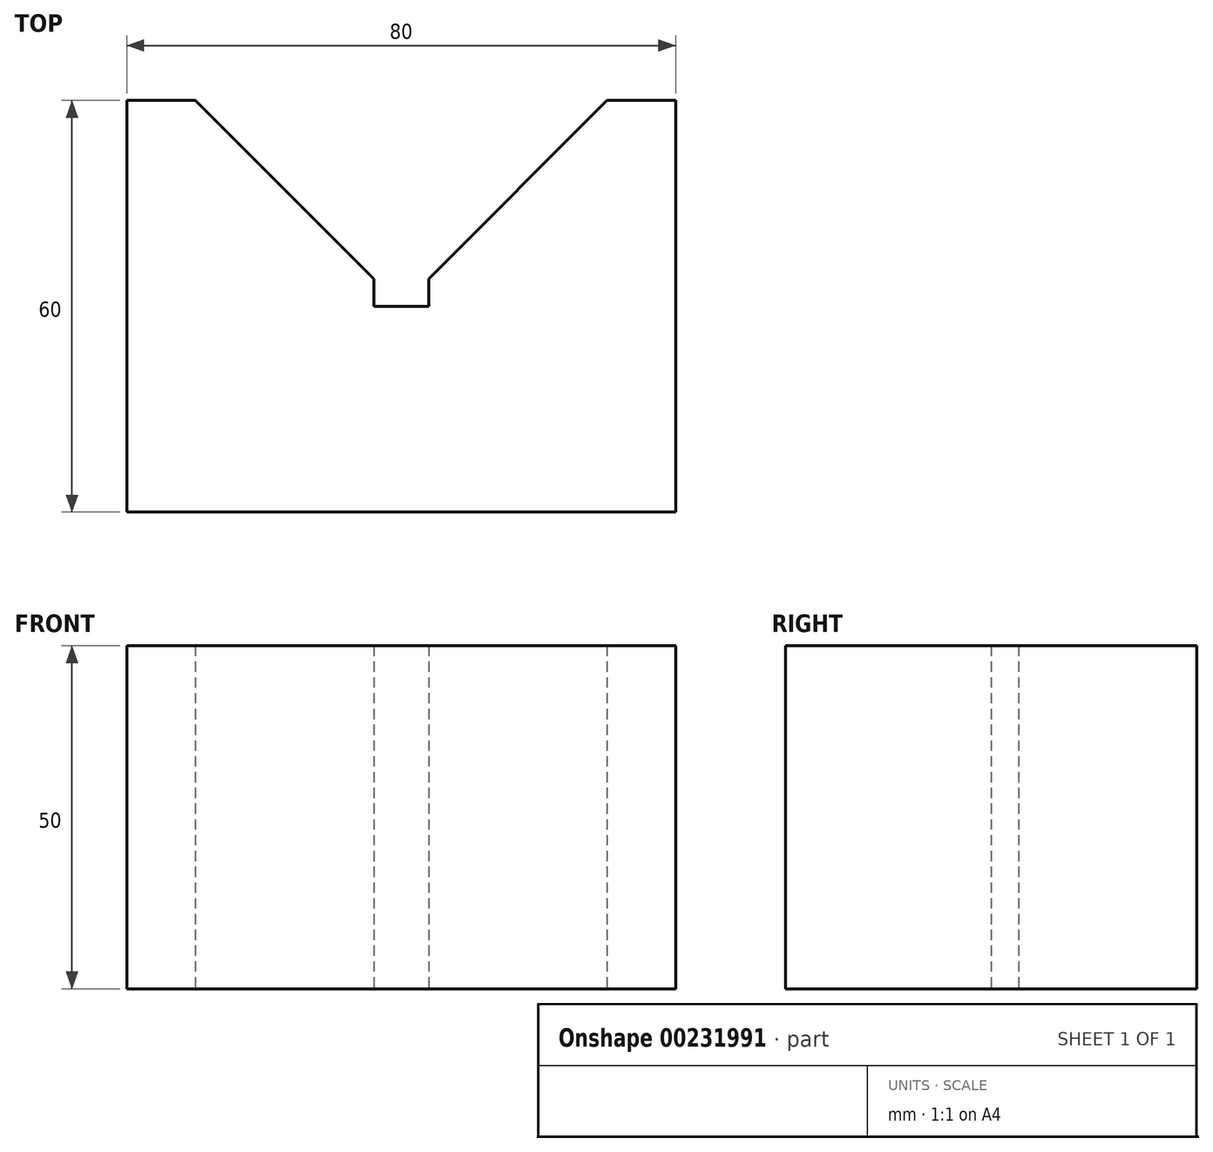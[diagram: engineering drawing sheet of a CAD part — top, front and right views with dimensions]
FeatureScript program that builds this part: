
annotation { "Feature Type Name" : "Feature", "Feature Type Description" : "" }
export const myFeature = defineFeature(function(context is Context, id is Id, definition is map)
    precondition{}
    {
        {
            var Q0;
            Q0=qCreatedBy(makeId("Top.planeOp"),FACE);
            var sketch = newSketch(context, id + "F0", { "sketchPlane" : qUnion([Q0])});
            skLineSegment(sketch, "E0", {"start": v(0, 0) * mm, "end": v(-40, 0) * mm});
            skLineSegment(sketch, "E1", {"start": v(-40, 0) * mm, "end": v(-40, 60) * mm});
            skLineSegment(sketch, "E2", {"start": v(-40, 60) * mm, "end": v(-30, 60) * mm});
            skLineSegment(sketch, "E3", {"start": v(-30, 60) * mm, "end": v(-4, 34) * mm});
            skLineSegment(sketch, "E4", {"start": v(-4, 34) * mm, "end": v(-4, 30) * mm});
            skLineSegment(sketch, "E5", {"start": v(-4, 30) * mm, "end": v(0, 30) * mm});
            skLineSegment(sketch, "E6.MirrorCS", {"start": v(4, 34) * mm, "end": v(4, 30) * mm});
            skLineSegment(sketch, "E7.MirrorCS", {"start": v(4, 30) * mm, "end": v(0, 30) * mm});
            skLineSegment(sketch, "E8.MirrorCS", {"start": v(0, 0) * mm, "end": v(40, 0) * mm});
            skLineSegment(sketch, "E9.MirrorCS", {"start": v(40, 60) * mm, "end": v(30, 60) * mm});
            skLineSegment(sketch, "E10.MirrorCS", {"start": v(40, 0) * mm, "end": v(40, 60) * mm});
            skLineSegment(sketch, "E11.MirrorCS", {"start": v(30, 60) * mm, "end": v(4, 34) * mm});
            skSolve(sketch);
        }
        {
            var Q0;
            Q0=makeQuery(id+"F0.imprint","IMPRINT",FACE,{"disambiguationData":[TD([[makeQuery(id+"F0.imprint","IMPRINT",EDGE,{"derivedFrom":sQuery(id+"F0.wireOp",EDGE,"E0")}),-1.0]])]});
            extrude(context, id + "F1", {"entities" : qUnion([Q0]), "depth" : 50 * mm});
        }
    });
